# Revit family: LWS
name_source: partatom
category: Lighting Fixtures
revit_build: Autodesk Revit Architecture 2012 (Build: 20110309_2315(x64)
units: mm (PartAtom-declared; Revit-internal decimal feet)

## types (1)
- LWS
    Apparent Load = 87 VA
    Default Elevation = 48 "
    Description = 16 inch x 24 inch LED Wrap Suspended High Bay/Low Bay.
    Is 120V = No
    Is 277V = Yes
    Lamp = LED Lamp
    Length = 24 "
    Load Classification = Lighting
    Manufacturer = Columbia Lighting
    Manufacturer Fax = 866-898-1065
    Material Finish = Hubbell - Paint - White
    Model = LWS
    Opal lens = Hubbell - Glass
    Pendant Height = 18 "
    Photometric Web = Web LWS : LWS-40XL-W-EDU
    Product Documentation Link = http://cdn.columbialighting.com
    Product Page URL = http://www.columbialighting.com
    URL = http://www.columbialighting.com
    Voltage = 277 V
    Wattage Comments = 87W-163W
    Watts = 87 W

## geometry (parser evidence)
native form markers: Sweep x5
no freeform markers — native parametric forms only
